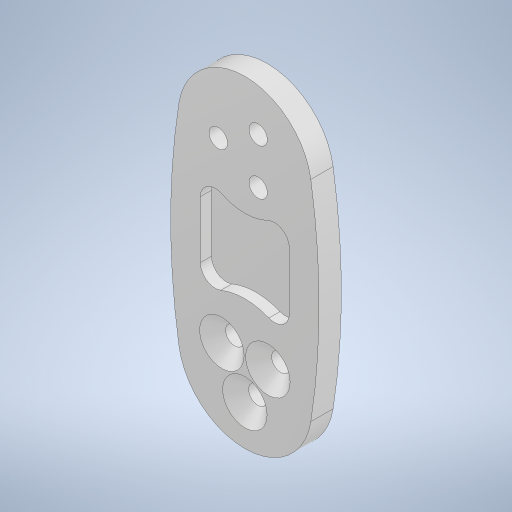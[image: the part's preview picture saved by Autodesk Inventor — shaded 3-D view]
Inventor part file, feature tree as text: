
AUTODESK INVENTOR PART (.ipt)
format: ipt  version: 2023.1 (Build 271208000, 208)  size: 332,800 bytes
history: native  units: mm
features: extrude x2, sketch x2, chamfer x1, fillet x1, projected_geometry x1
ambient origin geometry x8: Origin, YZ Plane, XZ Plane, XY Plane, X Axis, Y Axis, Z Axis, Center Point
bodies: Solid1 (feature_tree)
feature tree (7):
  extrude  "Extrusion1"  Depth=3.0mm TaperAngle=0.0deg
  chamfer  "Chamfer1"  Distance=2.0mm Angle=45.0deg
  extrude  "Extrusion2"  Depth=2.0mm
  fillet  "フィレット1"  Radius=14.0mm
  sketch  "Sketch2"  dims[d17=30.0mm d19=30.0mm d20=18.0mm d21=18.0mm d22=90.0deg d23=2.5mm d24=6.2mm d25=360.0deg d26=2.5mm d27=360.0deg d28=6.2mm d29=9.0mm d31=10.0mm d32=3.0mm d33=0.0mm d34=1.75mm d35=2.0mm d36=45.0deg]
  sketch  "Sketch3"  dims[d46=1.5mm d47=0.0mm d49=17.0mm d50=14.0mm d51=4.0mm d52=4.0mm d53=2.0mm]
  projected_geometry  "投影ループ3"
